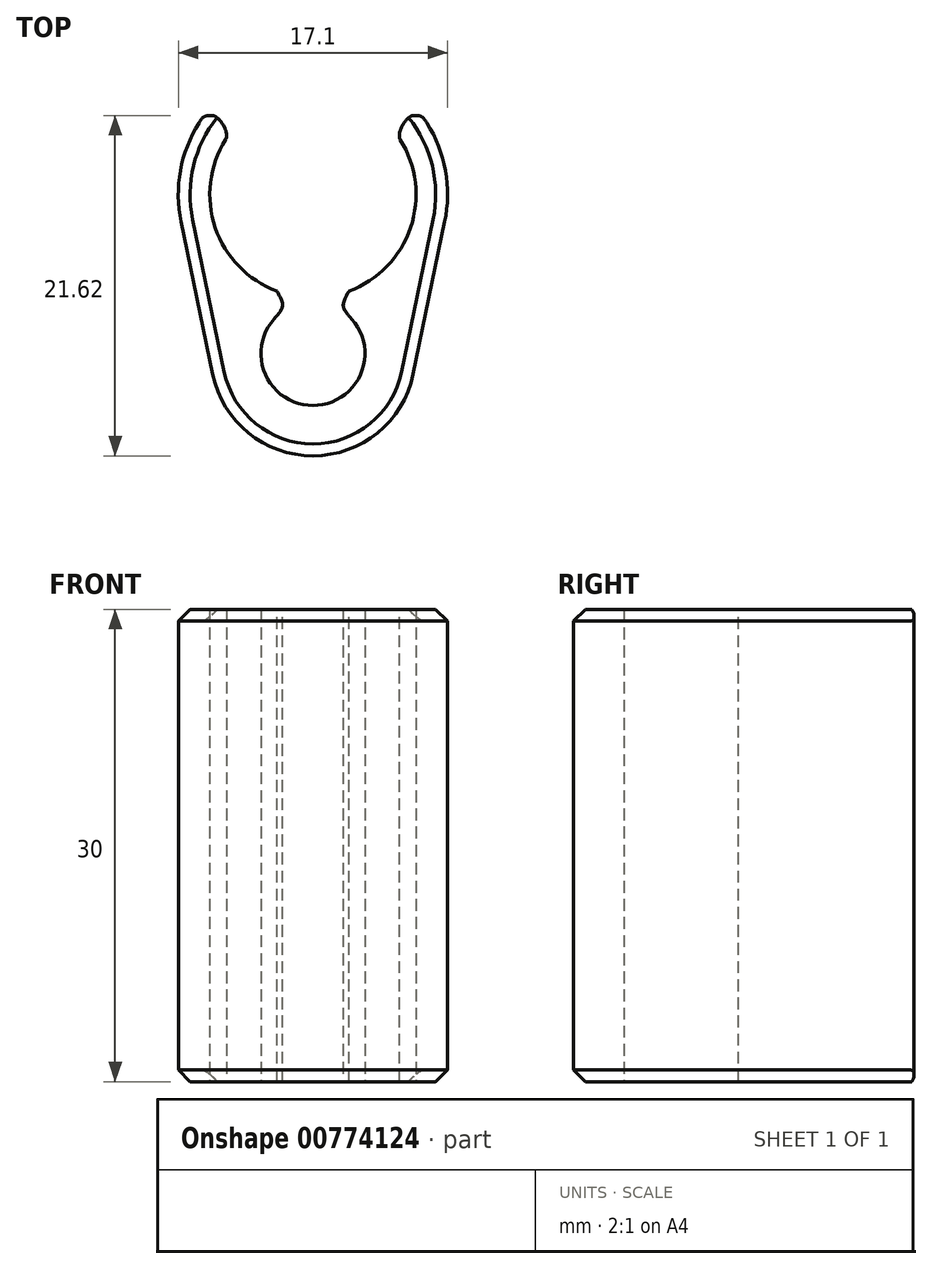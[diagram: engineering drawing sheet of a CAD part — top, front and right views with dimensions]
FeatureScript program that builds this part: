
annotation { "Feature Type Name" : "Feature", "Feature Type Description" : "" }
export const myFeature = defineFeature(function(context is Context, id is Id, definition is map)
    precondition{}
    {
        {
            var Q0;
            Q0=qCreatedBy(makeId("Top.planeOp"),FACE);
            var sketch = newSketch(context, id + "F0", { "sketchPlane" : qUnion([Q0]), "disableImprinting" : false});
            skCircle(sketch, "E0", {"center": v(0, 0) * mm, "radius": 3.3 * mm});
            skCircle(sketch, "E1", {"center": v(0, 10.1) * mm, "radius": 6.55 * mm, "construction": true});
            skLineSegment(sketch, "E2", {"start": v(0, 10.1) * mm, "end": v(0, 3.55) * mm, "construction": true});
            skLineSegment(sketch, "E3", {"start": v(0, 3.55) * mm, "end": v(0, 3.3) * mm, "construction": true});
            skLineSegment(sketch, "E4", {"start": v(0, 3.3) * mm, "end": v(0, 0) * mm, "construction": true});
            skArc(sketch, "E5", {"start": v(-4.21, 15.12) * mm, "mid": v(0, 3.55) * mm, "end": v(4.21, 15.12) * mm});
            skLineSegment(sketch, "E6", {"start": v(-4.21, 15.12) * mm, "end": v(0, 10.1) * mm, "construction": true});
            skLineSegment(sketch, "E7", {"start": v(4.21, 15.12) * mm, "end": v(0, 10.1) * mm, "construction": true});
            skLineSegment(sketch, "E8", {"start": v(4.21, 15.12) * mm, "end": v(6.92, 15.12) * mm});
            skLineSegment(sketch, "E9", {"start": v(-4.21, 15.12) * mm, "end": v(-6.92, 15.12) * mm});
            skArc(sketch, "E10", {"start": v(-6.92, 15.12) * mm, "mid": v(-8.36, 11.9) * mm, "end": v(-8.37, 8.36) * mm});
            skArc(sketch, "E11", {"start": v(8.37, 8.36) * mm, "mid": v(8.36, 11.9) * mm, "end": v(6.92, 15.12) * mm});
            skArc(sketch, "E12", {"start": v(-6.36, -1.32) * mm, "mid": v(0, -6.5) * mm, "end": v(6.36, -1.32) * mm});
            skLineSegment(sketch, "E13", {"start": v(-6.36, -1.32) * mm, "end": v(-8.37, 8.36) * mm});
            skLineSegment(sketch, "E14", {"start": v(8.37, 8.36) * mm, "end": v(6.36, -1.32) * mm});
            skSolve(sketch);
        }
        {
            var Q0;
            Q0=qSketchRegion(id+"F0",true);
            extrude(context, id + "F1", {"entities" : qUnion([Q0]), "depth" : 30 * mm, "offsetDistance" : 25 * mm});
        }
        {
            var Q0;
            Q0=makeQuery(id+"F1.opExtrude","SWEPT_EDGE",EDGE,{"disambiguationData":[OSD([sQuery(id+"F0.wireOp",EDGE,"E5"),sQuery(id+"F0.wireOp",EDGE,"E8")])]});
            var Q1;
            Q1=makeQuery(id+"F1.opExtrude","SWEPT_EDGE",EDGE,{"disambiguationData":[OSD([sQuery(id+"F0.wireOp",EDGE,"E5"),sQuery(id+"F0.wireOp",EDGE,"E9")])]});
            fillet(context, id + "F2", {"entities" : qUnion([Q0, Q1]), "tangentPropagation" : true, "crossSection" : FilletCrossSection.CONIC, "radius" : 1 * mm, "rho" : .2, "defaultsChanged" : true, "vertexSettings" : [], "allowEdgeOverflow" : false});
        }
        {
            var Q0;
            Q0=makeQuery(id+"F1.opExtrude","SWEPT_EDGE",EDGE,{"disambiguationData":[OSD([sQuery(id+"F0.wireOp",EDGE,"E9"),sQuery(id+"F0.wireOp",EDGE,"E10")])]});
            var Q1;
            Q1=makeQuery(id+"F1.opExtrude","SWEPT_EDGE",EDGE,{"disambiguationData":[OSD([sQuery(id+"F0.wireOp",EDGE,"E8"),sQuery(id+"F0.wireOp",EDGE,"E11")])]});
            fillet(context, id + "F3", {"entities" : qUnion([Q0, Q1]), "tangentPropagation" : true, "crossSection" : FilletCrossSection.CONIC, "radius" : 1 * mm, "rho" : .7, "defaultsChanged" : true, "vertexSettings" : [], "allowEdgeOverflow" : false});
        }
        {
            var Q0;
            Q0=makeQuery(id+"F1.opExtrude","CAP_EDGE",EDGE,{"disambiguationData":[OSD([sQuery(id+"F0.wireOp",EDGE,"E13")])],"isStart":false});
            var Q1;
            Q1=makeQuery(id+"F1.opExtrude","CAP_EDGE",EDGE,{"disambiguationData":[OSD([sQuery(id+"F0.wireOp",EDGE,"E14")])],"isStart":false});
            var Q2;
            Q2=makeQuery(id+"F1.opExtrude","CAP_EDGE",EDGE,{"disambiguationData":[OSD([sQuery(id+"F0.wireOp",EDGE,"E12")])],"isStart":false});
            var Q3;
            Q3=makeQuery(id+"F1.opExtrude","CAP_EDGE",EDGE,{"disambiguationData":[OSD([sQuery(id+"F0.wireOp",EDGE,"E11")])],"isStart":false});
            var Q4;
            Q4=makeQuery(id+"F1.opExtrude","CAP_EDGE",EDGE,{"disambiguationData":[OSD([sQuery(id+"F0.wireOp",EDGE,"E10")])],"isStart":false});
            var Q5;
            Q5=makeQuery(id+"F1.opExtrude","CAP_EDGE",EDGE,{"disambiguationData":[OSD([sQuery(id+"F0.wireOp",EDGE,"E10")])],"isStart":true});
            var Q6;
            Q6=makeQuery(id+"F1.opExtrude","CAP_EDGE",EDGE,{"disambiguationData":[OSD([sQuery(id+"F0.wireOp",EDGE,"E13")])],"isStart":true});
            var Q7;
            Q7=makeQuery(id+"F1.opExtrude","CAP_EDGE",EDGE,{"disambiguationData":[OSD([sQuery(id+"F0.wireOp",EDGE,"E12")])],"isStart":true});
            var Q8;
            Q8=makeQuery(id+"F1.opExtrude","CAP_EDGE",EDGE,{"disambiguationData":[OSD([sQuery(id+"F0.wireOp",EDGE,"E14")])],"isStart":true});
            var Q9;
            Q9=makeQuery(id+"F1.opExtrude","CAP_EDGE",EDGE,{"disambiguationData":[OSD([sQuery(id+"F0.wireOp",EDGE,"E11")])],"isStart":true});
            chamfer(context, id + "F4", {"entities" : qUnion([Q0, Q1, Q2, Q3, Q4, Q5, Q6, Q7, Q8, Q9]), "width" : .75 * mm});
        }
        {
            var Q0;
            Q0=makeQuery(id+"F1.opExtrude","CAP_FACE",FACE,{"disambiguationData":[OSD([sQuery(id+"F0.wireOp",EDGE,"E0"),sQuery(id+"F0.wireOp",EDGE,"E5"),sQuery(id+"F0.wireOp",EDGE,"E8"),sQuery(id+"F0.wireOp",EDGE,"E9"),sQuery(id+"F0.wireOp",EDGE,"E10"),sQuery(id+"F0.wireOp",EDGE,"E11"),sQuery(id+"F0.wireOp",EDGE,"E12"),sQuery(id+"F0.wireOp",EDGE,"E13"),sQuery(id+"F0.wireOp",EDGE,"E14")])],"isStart":false});
            var sketch = newSketch(context, id + "F5", { "sketchPlane" : qUnion([Q0])});
            skLineSegment(sketch, "E15", {"start": v(0, 0) * mm, "end": v(-2.29, 3.96) * mm});
            skLineSegment(sketch, "E16", {"start": v(-2.29, 3.96) * mm, "end": v(2.29, 3.96) * mm});
            skLineSegment(sketch, "E17", {"start": v(2.29, 3.96) * mm, "end": v(0, 0) * mm});
            skLineSegment(sketch, "E18", {"start": v(0, 0) * mm, "end": v(0, 3.96) * mm, "construction": true});
            skPoint(sketch, "E18.endSnap0", {"position": v(0, 3.55) * mm});
            skSolve(sketch);
        }
        {
            var Q0;
            Q0 = qSketchRegion(id + "F5", true);
            extrude(context, id + "F6", {"entities" : qUnion([Q0]), "operationType" : NewBodyOperationType.REMOVE, "endBound" : BoundingType.THROUGH_ALL, "oppositeDirection" : true, "depth" : 25 * mm, "offsetDistance" : 25 * mm});
        }
        {
            var Q0;
            Q0=makeQuery(id+"F6.boolean.opBoolean","COPY",EDGE,{"derivedFrom":makeQuery(id+"F6.opExtrude","SWEPT_EDGE",EDGE,{"disambiguationData":[OSD([sQuery(id+"F0.wireOp",EDGE,"E5"),sQuery(id+"F5.wireOp",EDGE,"E15"),sQuery(id+"F5.wireOp",EDGE,"E16")])]})});
            var Q1;
            Q1=makeQuery(id+"F6.boolean.opBoolean","INTERSECT",EDGE,{"derivedFrom":[makeQuery(id+"F1.opExtrude","SWEPT_FACE",FACE,{"disambiguationData":[OSD([sQuery(id+"F0.wireOp",EDGE,"E0")])]}),makeQuery(id+"F6.opExtrude","SWEPT_FACE",FACE,{"disambiguationData":[OSD([sQuery(id+"F5.wireOp",EDGE,"E15")])]})]});
            var Q2;
            Q2=makeQuery(id+"F6.boolean.opBoolean","INTERSECT",EDGE,{"derivedFrom":[makeQuery(id+"F1.opExtrude","SWEPT_FACE",FACE,{"disambiguationData":[OSD([sQuery(id+"F0.wireOp",EDGE,"E0")])]}),makeQuery(id+"F6.opExtrude","SWEPT_FACE",FACE,{"disambiguationData":[OSD([sQuery(id+"F5.wireOp",EDGE,"E17")])]})]});
            var Q3;
            Q3=makeQuery(id+"F6.boolean.opBoolean","COPY",EDGE,{"derivedFrom":makeQuery(id+"F6.opExtrude","SWEPT_EDGE",EDGE,{"disambiguationData":[OSD([sQuery(id+"F0.wireOp",EDGE,"E5"),sQuery(id+"F5.wireOp",EDGE,"E16"),sQuery(id+"F5.wireOp",EDGE,"E17")])]})});
            fillet(context, id + "F7", {"entities" : qUnion([Q0, Q1, Q2, Q3]), "tangentPropagation" : true, "crossSection" : FilletCrossSection.CONIC, "radius" : 1.5 * mm, "rho" : .7, "defaultsChanged" : true, "vertexSettings" : [], "allowEdgeOverflow" : false});
        }
    });
